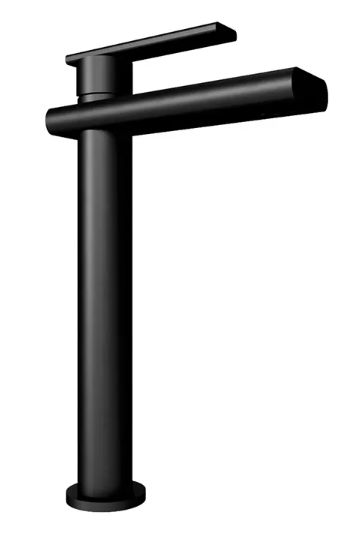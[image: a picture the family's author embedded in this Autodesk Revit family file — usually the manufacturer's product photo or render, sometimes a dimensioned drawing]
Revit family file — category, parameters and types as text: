
# Revit family: EP-938-EB_RFA
name_source: partatom
category: Aparatos sanitarios
units: mm (PartAtom-declared; Revit-internal decimal feet)

## family parameters
Activar corte en vistas = No
Compartido = Sí
Corte con vacíos al cargar = No
Cota de conector redondo = Usar diámetro
Mantener orientación de anotación = No
Número OmniClass = 23.45.55.14
Punto de cálculo de habitación = Sí
Se basa en plano de trabajo = Sí
Siempre vertical = Sí
Tipo de pieza = Normal
Título OmniClass = Single Faucets

## types (1)
- EP-938-EB
    Accesorios = Inserto, herramienta de sujeción
    Características del Producto = Monomando de lavabo alto con contra de push Premier Ébano
    Comentarios de tipo = Incluye contra de push. Incluye inserto para usarse con lavabos sin rebosadero.
    Cuerpo de Latón = Brass
    Descripción = Monomando de lavabo alto con contra de push Premier Ébano
    Elevación por defecto = 1"
    Fabricante = HELVEX S.A. de C.V.
    Garantía = El producto HELVEX está garantizado, en lo que
se refiere a los acabados, por 10 axos para los
acabados cromo y duravex, y por 2 axos en
acabados diferentes al cromo y duravex.
Las piezas que sufren de desgaste natural en el
producto estin garantizadas para uso residencial
por 5 axos, y para uso comercial por 3 axos.
La vigencia de la garantia inicia a partir de la
fecha de entrega del producto al consumidor
indicada en esta Poliza de Garantta
    Imagen de tipo = EP-938-EB.png
    Instalación = Conexión ½ - 14 NPSM
    Modelo = EP-938-EB
    Operación = El maneral tienen una rotación horizontal para la función de agua caliente y fría; y vertical para abrir y cerrar el flujo de agua.
    Presión Máxima de Trabajo = 85.3 psi
    Presión Mínima de Trabajo = 9.9 psi
    Total Depth = 7"
    Total Height = 12"
    Total Width = 2"
    URL = https://helvex.com.mx
    Ébano = Ébano

## geometry (parser evidence)
native form markers: Sweep x3
no freeform markers — native parametric forms only
